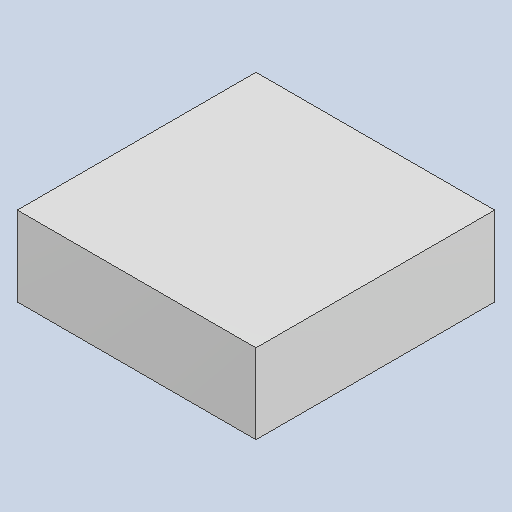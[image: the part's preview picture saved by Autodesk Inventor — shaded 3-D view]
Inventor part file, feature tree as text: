
AUTODESK INVENTOR PART (.ipt)
format: ipt  version: 2023.4 (Build 274418000, 418)  size: 79,872 bytes
history: native  units: mm
features: extrude x1
ambient origin geometry x8: Origin, YZ Plane, XZ Plane, XY Plane, X Axis, Y Axis, Z Axis, Center Point
bodies: Solid1 (feature_tree)
feature tree (1):
  extrude  "Extruded_20"  [1 undecoded]
note: 1 required parameter value undecoded (feature->parameter linkage not recoverable at this tier; creation-order binding heuristic only, values carry confidence <= 0.55)
